# Revit family: Genie_Site_ArticulatingBoom_(S-65XC)1
name_source: partatom
category: Site
revit_build: Autodesk Revit 2017 (Build: 20160225_1515(x64)
units: mm (PartAtom-declared; Revit-internal decimal feet)

## family parameters
Always vertical = Yes
Cut with Voids When Loaded = No
OmniClass Number = 23.50.85.17
OmniClass Title = Telescoping Platforms
Part Type = Normal
Round Connector Dimension = Use Diameter
Shared = No
Work Plane-Based = No

## types (1)
- S-65XC
    Assembly Code = E1030900
    AssetType = Fixed
    BIMObjectName = Genie_Site_ArticulatingBoom_(S-65XC)
    ClassificationName = Uniclass2015
    ClassificationValue = Pr_65_80_47_95
    Color = Grey & Blue
    Cost = 0 $
    Description = S-65 XC telescopic boom lifts are the redesigned Xtra Capacity™ version of the popular Genie S-60 and S-65. They can perform a wider range of heavier lift tasks on construction and industrial jobsites thanks to their dual lift capacity and offer innovative features to help increase jobsite efficiency.
    DocumentationLiterature = https://www.genielift.com
    DocumentationTechnical = https://www.genielift.com
    DurationUnit = Years
    ExpectedLife = 0
    Features = Full-time active oscillating axle and full-time positive traction for superior terrainability. Chassis tilt sensor technology  maximizes access to hard-to-reach work areas. 1.52 m (5 ft) robust articulating jib. Dual lifting capacity of 300 kg (660 lb) and 454 kg (1,000 lb) to lift increased loads and up to 3 operators. Automatic envelope control technology for a smooth operating envelope. Zero-load field calibration and onboard diagnostics maximize serviceability.
    Finish = Painted Steel
    IfcExportAs = IfcTransportElement
    IfcExportType = IfcTransportElementType
    Keynote = X
    Manufacturer = Genie
    ManufacturerName = Genie
    Material = Painted Steel
    Model = Genie - Articulating Boom
    ModelNumber = S-65XC
    ModelReference = Genie - Articulating Boom
    NBSDescription = Vertical lifting platforms
    NBSObjectName = Genie - Vertical lifting platforms
    NBSReference = 90-80-65/350
    NominalDepth = 2490 mm
    NominalHeight = 2820 mm  [stored 9.25197 ft]
    NominalLength = 9700 mm
    ProductionYear = 2018
    ReplacementCost = 0
    Size = 2.49m x 2.82m x 9.7m
    Type Comments = S-65XC
    TypeName = Genie - Articulating Boom
    URL = http://www.genielift.co.uk
    WarrantyDurationLabor = 0
    WarrantyDurationParts = 0
    WarrantyDurationUnit = Years
    WarrantyGuarantorLabor = http://www.genielift.co.uk
    WarrantyGuarantorParts = http://www.genielift.co.uk
    _BSBibleVersion = 15
    _BimSpecGuid = 0
    _CurrentRevision = 1
    _DistributedBy = www.bimstore.co.uk

note: [stored X ft] marks values corroborated as IEEE doubles in the binary element streams (Revit-internal decimal feet)

## geometry (parser evidence)
native form markers: Sweep x33
no freeform markers — native parametric forms only
